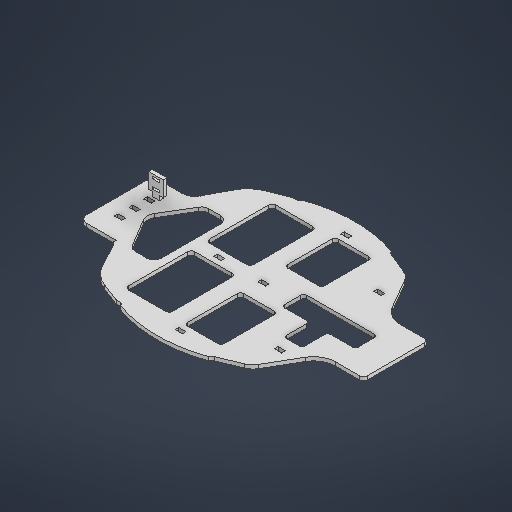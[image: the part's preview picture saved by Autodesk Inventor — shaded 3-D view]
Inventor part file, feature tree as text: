
AUTODESK INVENTOR PART (.ipt)
format: ipt  version: 2025.3 (Build 293356000, 356)  size: 524,288 bytes
history: native  units: in
note: dims shown in document units (in); Inventor stores cm internally (conversion verified against a paired STEP export)
features: extrude x3, sketch x2, projected_geometry x2, other x2, reference x1
ambient origin geometry x8: Origin, YZ Plane, XZ Plane, XY Plane, X Axis, Y Axis, Z Axis, Center Point
bodies: Solid1 (feature_tree), Solid2 (feature_tree), Body1 (feature_tree), Body2 (feature_tree)
feature tree (10):
  sketch  "Sketch1"  dims[d0=0.3937in d1=0.1969in]
  extrude  "Extrusion1"  Depth=0.1969in
  extrude  "Extrusion2"  Depth=0.3937in TaperAngle=0.0deg
  extrude  "Extrusion3"  Depth=0.3937in TaperAngle=0.0deg
  projected_geometry  "Projected Loop1"
  sketch  "Sketch2"  dims[d2=0.3937in d3=0.3937in d4=0.0in d5=0.3937in d6=0.0in d7=0.1575in d8=2.3622in d9=0.3937in d10=0.0in]
  reference  "Reference1"
  projected_geometry  "Projected Loop2"
  other  "Assembly2.iam"
  other  "base botellas:1"
